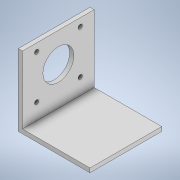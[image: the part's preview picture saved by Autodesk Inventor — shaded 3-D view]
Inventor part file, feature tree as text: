
AUTODESK INVENTOR PART (.ipt)
format: ipt  version: 2022 (Build 260153000, 153)  size: 116,224 bytes
history: native  units: mm
features: extrude x2, sketch x2
ambient origin geometry x8: Origin, YZ Plane, XZ Plane, XY Plane, X Axis, Y Axis, Z Axis, Center Point
bodies: Solid1 (feature_tree)
feature tree (4):
  extrude  "Extrusion1"  Depth=3.0mm
  extrude  "Extrusion2"  Depth=48.0mm
  sketch  "Sketch1"  dims[d0=51.0mm d1=3.0mm]
  sketch  "Sketch2"  dims[d2=48.0mm d3=48.0mm d4=51.0mm d5=0.0mm d7=22.0mm d12=3.0mm d13=3.0mm d14=51.0mm d15=0.0mm]
